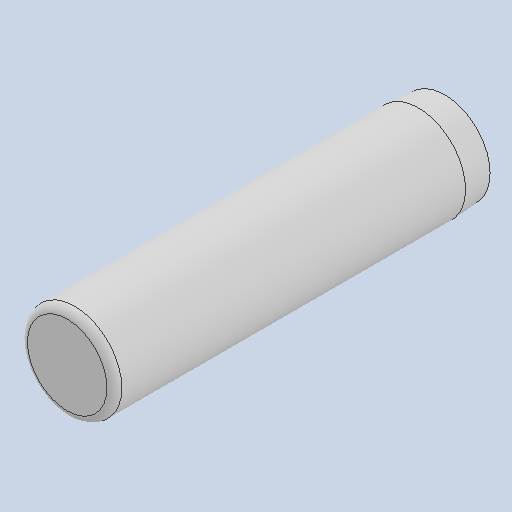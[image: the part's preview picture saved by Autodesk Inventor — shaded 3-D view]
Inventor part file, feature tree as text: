
AUTODESK INVENTOR PART (.ipt)
format: ipt  version: 2022 (Build 260153000, 153)  size: 94,720 bytes
history: native  units: in
note: dims shown in document units (in); Inventor stores cm internally (conversion verified against a paired STEP export)
features: chamfer x1
ambient origin geometry x8: Origin, YZ Plane, XZ Plane, XY Plane, X Axis, Y Axis, Z Axis, Center Point
bodies: Solid1 (feature_tree)
feature tree (1):
  chamfer  "Chamfer1"  [1 undecoded]
note: 1 required parameter value undecoded (feature->parameter linkage not recoverable at this tier; creation-order binding heuristic only, values carry confidence <= 0.55)
